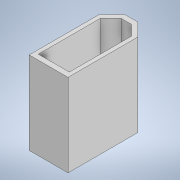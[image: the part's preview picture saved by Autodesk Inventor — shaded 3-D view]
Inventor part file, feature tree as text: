
AUTODESK INVENTOR PART (.ipt)
format: ipt  version: 2020 (Build 240168000, 168)  size: 116,736 bytes
history: native  units: mm
features: extrude x2, sketch x2
ambient origin geometry x8: Origin, YZ Plane, XZ Plane, XY Plane, X Axis, Y Axis, Z Axis, Center Point
bodies: Solid1 (feature_tree)
feature tree (4):
  extrude  "Extrusion1"  Depth=7.5mm
  extrude  "Extrusion2"  Depth=8.0mm
  sketch  "Sketch1"  dims[d0=7.5mm d1=3.75mm]
  sketch  "Sketch2"  dims[d2=16.0mm d3=8.0mm d4=2.5mm d5=135.0deg d6=135.0deg d7=16.0mm d8=0.0mm d9=14.0mm d10=2.0mm d11=7.0mm d12=6.0mm d13=3.0mm d14=8.0mm d15=0.0mm]
